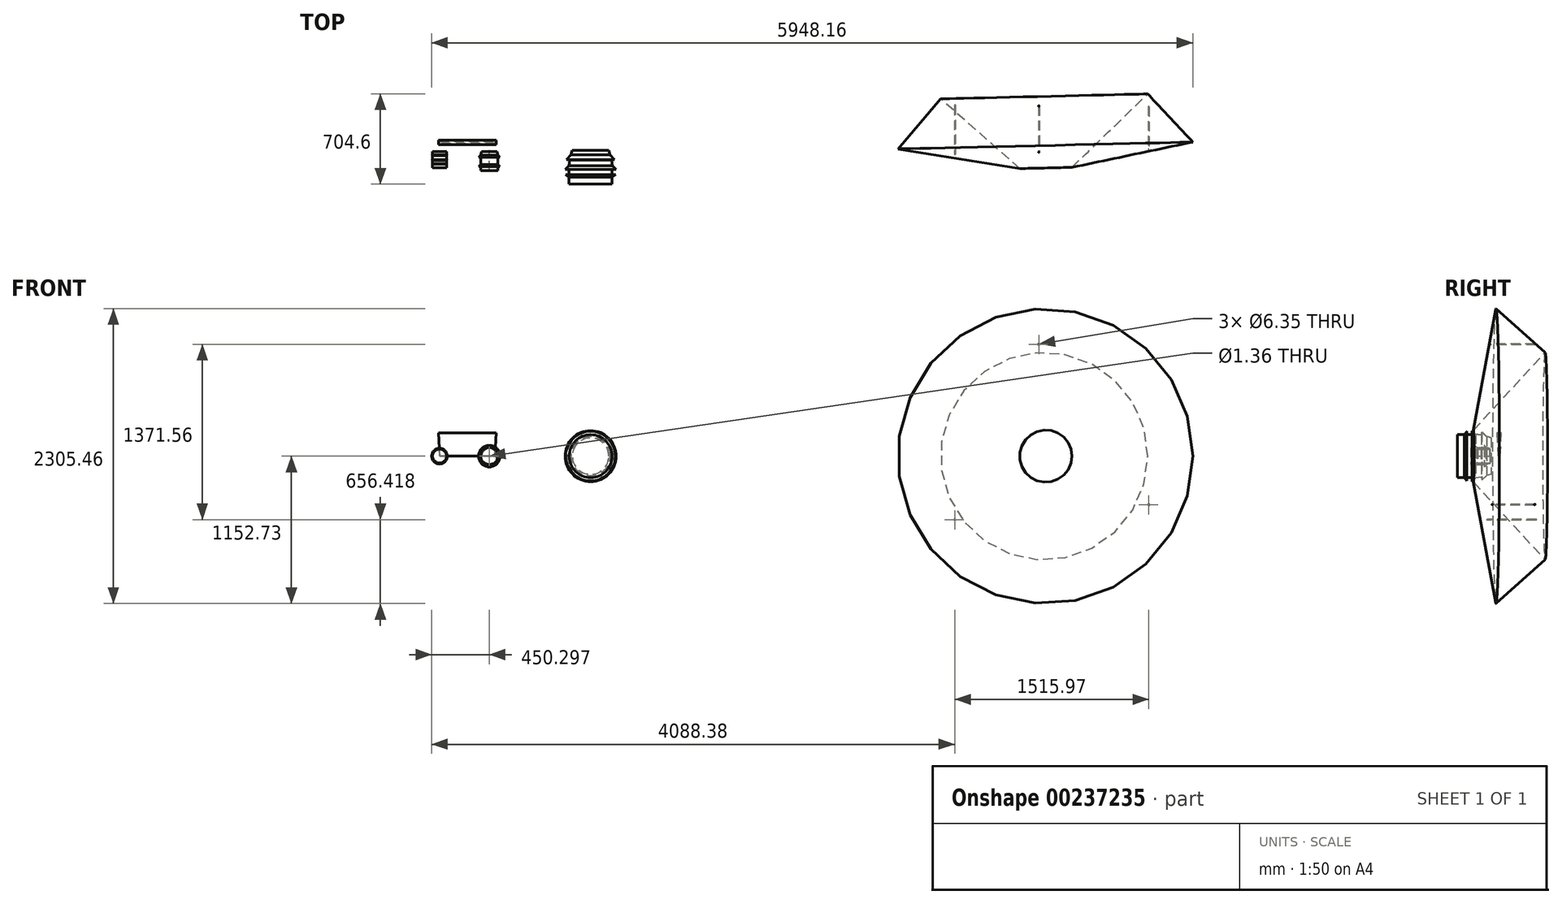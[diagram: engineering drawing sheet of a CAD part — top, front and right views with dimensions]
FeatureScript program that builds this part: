
annotation { "Feature Type Name" : "Feature", "Feature Type Description" : "" }
export const myFeature = defineFeature(function(context is Context, id is Id, definition is map)
    precondition{}
    {
        {
            var Q0;
            Q0=qCreatedBy(makeId("Top.planeOp"),FACE);
            var sketch = newSketch(context, id + "F0", { "sketchPlane" : qUnion([Q0])});
            skLineSegment(sketch, "E0", {"start": v(0, 61.32) * mm, "end": v(0, -63.64) * mm});
            skLineSegment(sketch, "E1", {"start": v(0, -63.64) * mm, "end": v(-54.78, -63.64) * mm});
            skLineSegment(sketch, "E2", {"start": v(-54.78, -63.64) * mm, "end": v(-54.78, -37.28) * mm});
            skLineSegment(sketch, "E3", {"start": v(-54.78, -37.28) * mm, "end": v(-61.08, -37.28) * mm});
            skLineSegment(sketch, "E4", {"start": v(-61.08, -37.28) * mm, "end": v(-54.78, -31.83) * mm});
            skLineSegment(sketch, "E5", {"start": v(-54.78, -31.83) * mm, "end": v(-54.78, -6.3) * mm});
            skLineSegment(sketch, "E6", {"start": v(-54.78, -6.3) * mm, "end": v(-61.4, -6.3) * mm});
            skLineSegment(sketch, "E7", {"start": v(-61.4, -6.3) * mm, "end": v(-54.86, 0) * mm});
            skLineSegment(sketch, "E8", {"start": v(-54.86, 0) * mm, "end": v(-54.86, 30.63) * mm});
            skLineSegment(sketch, "E9", {"start": v(-54.86, 30.63) * mm, "end": v(-61, 30.63) * mm});
            skLineSegment(sketch, "E10", {"start": v(-61, 30.63) * mm, "end": v(-54.39, 37.78) * mm});
            skLineSegment(sketch, "E11", {"start": v(-54.39, 37.78) * mm, "end": v(-54.39, 61.86) * mm});
            skLineSegment(sketch, "E12", {"start": v(-54.39, 61.86) * mm, "end": v(0, 61.32) * mm});
            skSolve(sketch);
        }
        {
            var Q0;
            Q0 = qSketchRegion(id + "F0", true);
            var Q1;
            Q1=sQuery(id+"F0.wireOp",EDGE,"E0");
            revolve(context, id + "F9", {"entities" : qUnion([Q0]), "axis" : qUnion([Q1]), "revolveType" : RevolveType.FULL});
        }
        {
            var Q0;
            Q0=qCreatedBy(makeId("Top.planeOp"),FACE);
            var sketch = newSketch(context, id + "F1", { "sketchPlane" : qUnion([Q0])});
            skLineSegment(sketch, "E13", {"start": v(388.23, 65.34) * mm, "end": v(388.23, -86.93) * mm});
            skLineSegment(sketch, "E14", {"start": v(388.23, -86.93) * mm, "end": v(321.32, -86.93) * mm});
            skLineSegment(sketch, "E15", {"start": v(321.32, -86.93) * mm, "end": v(321.32, -54.31) * mm});
            skLineSegment(sketch, "E16", {"start": v(321.32, -54.31) * mm, "end": v(306.33, -54.31) * mm});
            skLineSegment(sketch, "E17", {"start": v(306.33, -54.31) * mm, "end": v(321.46, -40.18) * mm});
            skLineSegment(sketch, "E18", {"start": v(321.46, -40.18) * mm, "end": v(321.46, 17.56) * mm});
            skLineSegment(sketch, "E19", {"start": v(321.46, 17.56) * mm, "end": v(304.83, 17.56) * mm});
            skLineSegment(sketch, "E20", {"start": v(304.83, 17.56) * mm, "end": v(323.23, 33.91) * mm});
            skLineSegment(sketch, "E21", {"start": v(323.23, 33.91) * mm, "end": v(330.04, 61.17) * mm});
            skLineSegment(sketch, "E22", {"start": v(330.04, 61.17) * mm, "end": v(388.23, 65.34) * mm});
            skLineSegment(sketch, "E23", {"start": v(388.9, 128.63) * mm, "end": v(388.9, -142.29) * mm, "construction": true});
            skSolve(sketch);
        }
        {
            var Q0;
            Q0 = qSketchRegion(id + "F1", true);
            var Q1;
            Q1=sQuery(id+"F1.wireOp",EDGE,"E23");
            revolve(context, id + "F10", {"entities" : qUnion([Q0]), "axis" : qUnion([Q1]), "revolveType" : RevolveType.FULL});
        }
        {
            var Q0;
            Q0=qCreatedBy(makeId("Top.planeOp"),FACE);
            var sketch = newSketch(context, id + "F2", { "sketchPlane" : qUnion([Q0])});
            skLineSegment(sketch, "E24", {"start": v(1038.09, 71.69) * mm, "end": v(1180.64, 71.69) * mm});
            skLineSegment(sketch, "E25", {"start": v(1180.64, 71.69) * mm, "end": v(1180.64, -191.83) * mm});
            skLineSegment(sketch, "E26", {"start": v(1180.64, -191.83) * mm, "end": v(1012.72, -191.83) * mm});
            skLineSegment(sketch, "E27", {"start": v(1012.72, -191.83) * mm, "end": v(1012.72, -136.7) * mm});
            skLineSegment(sketch, "E28", {"start": v(1012.72, -136.7) * mm, "end": v(986.44, -118.4) * mm});
            skLineSegment(sketch, "E29", {"start": v(986.44, -118.4) * mm, "end": v(1012.42, -118.4) * mm});
            skLineSegment(sketch, "E30", {"start": v(1012.42, -118.4) * mm, "end": v(1012.42, -77.62) * mm});
            skLineSegment(sketch, "E31", {"start": v(1012.42, -77.62) * mm, "end": v(981.6, -77.62) * mm});
            skLineSegment(sketch, "E32", {"start": v(981.6, -77.62) * mm, "end": v(1010.6, -49.88) * mm});
            skLineSegment(sketch, "E33", {"start": v(1010.6, -49.88) * mm, "end": v(1016.64, -3.06) * mm});
            skLineSegment(sketch, "E34", {"start": v(1016.64, -3.06) * mm, "end": v(992.91, 0) * mm});
            skLineSegment(sketch, "E35", {"start": v(992.91, 0) * mm, "end": v(1027.82, 36.77) * mm});
            skLineSegment(sketch, "E36", {"start": v(1027.82, 36.77) * mm, "end": v(1038.09, 71.69) * mm});
            skSolve(sketch);
        }
        {
            var Q0;
            Q0 = qSketchRegion(id + "F2", true);
            var Q1;
            Q1=sQuery(id+"F2.wireOp",EDGE,"E25");
            revolve(context, id + "F11", {"entities" : qUnion([Q0]), "axis" : qUnion([Q1]), "revolveType" : RevolveType.FULL});
        }
        {
            var Q0;
            Q0=qCreatedBy(makeId("Top.planeOp"),FACE);
            var sketch = newSketch(context, id + "F3", { "sketchPlane" : qUnion([Q0])});
            skLineSegment(sketch, "E37.bottom", {"start": v(433.15, 143.15) * mm, "end": v(0.09, 143.15) * mm});
            skLineSegment(sketch, "E37.top", {"start": v(433.15, 124.86) * mm, "end": v(0.09, 124.86) * mm});
            skLineSegment(sketch, "E37.left", {"start": v(433.15, 143.15) * mm, "end": v(433.15, 124.86) * mm});
            skLineSegment(sketch, "E37.right", {"start": v(0.09, 143.15) * mm, "end": v(0.09, 124.86) * mm});
            skPoint(sketch, "E37.middle", {"position": v(216.62, 134) * mm});
            skSolve(sketch);
        }
        {
            var Q0;
            Q0=makeQuery(id+"F3.imprint","IMPRINT",FACE,{"disambiguationData":[TD([[makeQuery(id+"F3.imprint","IMPRINT",EDGE,{"derivedFrom":sQuery(id+"F3.wireOp",EDGE,"E37.bottom")}),1.0]])]});
            extrude(context, id + "F4", {"entities" : qUnion([Q0]), "depth" : 180.76 * mm, "hasDraft" : true, "draftAngle" : 3 * degree});
        }
        {
            var Q0;
            Q0=qCreatedBy(makeId("Top.planeOp"),FACE);
            var sketch = newSketch(context, id + "F5", { "sketchPlane" : qUnion([Q0])});
            skCircle(sketch, "E38", {"center": v(5039.49, -161.08) * mm, "radius": 512.65 * mm});
            skPoint(sketch, "E38.first.point", {"position": v(4534.83, -70.88) * mm});
            skPoint(sketch, "E38.second.point", {"position": v(4731.1, 248.45) * mm});
            skPoint(sketch, "E38.third.point", {"position": v(4750.65, -584.61) * mm});
            skCircle(sketch, "E39", {"center": v(4059.71, 14.03) * mm, "radius": 482.65 * mm});
            skPoint(sketch, "E39.first.point", {"position": v(3916, 474.79) * mm});
            skPoint(sketch, "E39.second.point", {"position": v(3581.95, 82.54) * mm});
            skLineSegment(sketch, "E40", {"start": v(3581.95, 82.54) * mm, "end": v(3916, 474.79) * mm});
            skLineSegment(sketch, "E41", {"start": v(4534.83, -70.88) * mm, "end": v(3581.95, 82.54) * mm});
            skLineSegment(sketch, "E42", {"start": v(3916, 474.79) * mm, "end": v(4534.83, -70.88) * mm});
            skLineSegment(sketch, "E43", {"start": v(4534.83, -70.88) * mm, "end": v(4731.1, 248.45) * mm});
            skLineSegment(sketch, "E44", {"start": v(4750.65, -584.61) * mm, "end": v(4731.1, 248.45) * mm});
            skLineSegment(sketch, "E45", {"start": v(4750.65, -584.61) * mm, "end": v(4534.83, -70.88) * mm});
            skSolve(sketch);
        }
        {
            var Q0;
            Q0=makeQuery(id+"F5.imprint","IMPRINT",FACE,{"disambiguationData":[TD([[makeQuery(id+"F5.imprint","IMPRINT",EDGE,{"derivedFrom":sQuery(id+"F5.wireOp",EDGE,"E40")}),-1.0]])]});
            var Q1;
            Q1=sQuery(id+"F5.wireOp",EDGE,"E44");
            revolve(context, id + "F6", {"entities" : qUnion([Q0]), "axis" : qUnion([Q1]), "revolveType" : RevolveType.FULL});
        }
        {
            var Q0;
            Q0=qCreatedBy(makeId("Front.planeOp"),FACE);
            var sketch = newSketch(context, id + "F7", { "sketchPlane" : qUnion([Q0])});
            skPoint(sketch, "E46", {"position": v(4683.32, 875.25) * mm});
            skPoint(sketch, "E47.1.0", {"position": v(5542.96, -378.93) * mm});
            skPoint(sketch, "E47.2.0", {"position": v(4026.99, -496.31) * mm});
            skPoint(sketch, "E47.center", {"position": v(4751.09, 0) * mm});
            skLineSegment(sketch, "E47.anchor1", {"start": v(4751.09, 0) * mm, "end": v(4683.32, 875.25) * mm, "construction": true});
            skLineSegment(sketch, "E47.anchor2", {"start": v(4751.09, 0) * mm, "end": v(4026.99, -496.31) * mm, "construction": true});
            skSolve(sketch);
        }
        {
            var Q0;
            Q0=sQuery(id+"F7.wireOp",VERTEX,"E47.anchor1.end");
            var Q1;
            Q1=sQuery(id+"F7.wireOp",VERTEX,"E47.2.0");
            var Q2;
            Q2=sQuery(id+"F7.wireOp",VERTEX,"E47.1.0");
            var Q3;
            Q3=makeQuery(id+"F6.opRevolve","SWEPT_BODY",BODY,{"disambiguationData":[OSD([sQuery(id+"F5.wireOp",EDGE,"E40"),sQuery(id+"F5.wireOp",EDGE,"E41"),sQuery(id+"F5.wireOp",EDGE,"E42")])]});
            hole(context, id + "F8", {"style" : HoleStyle.SIMPLE, "endStyle" : HoleEndStyle.THROUGH, "holeDiameter" : 6.35 * mm, "tappedDepth" : 12.7 * mm, "tapClearance" : 3, "locations" : qUnion([Q0, Q1, Q2]), "scope" : qUnion([Q3])});
        }
    });
